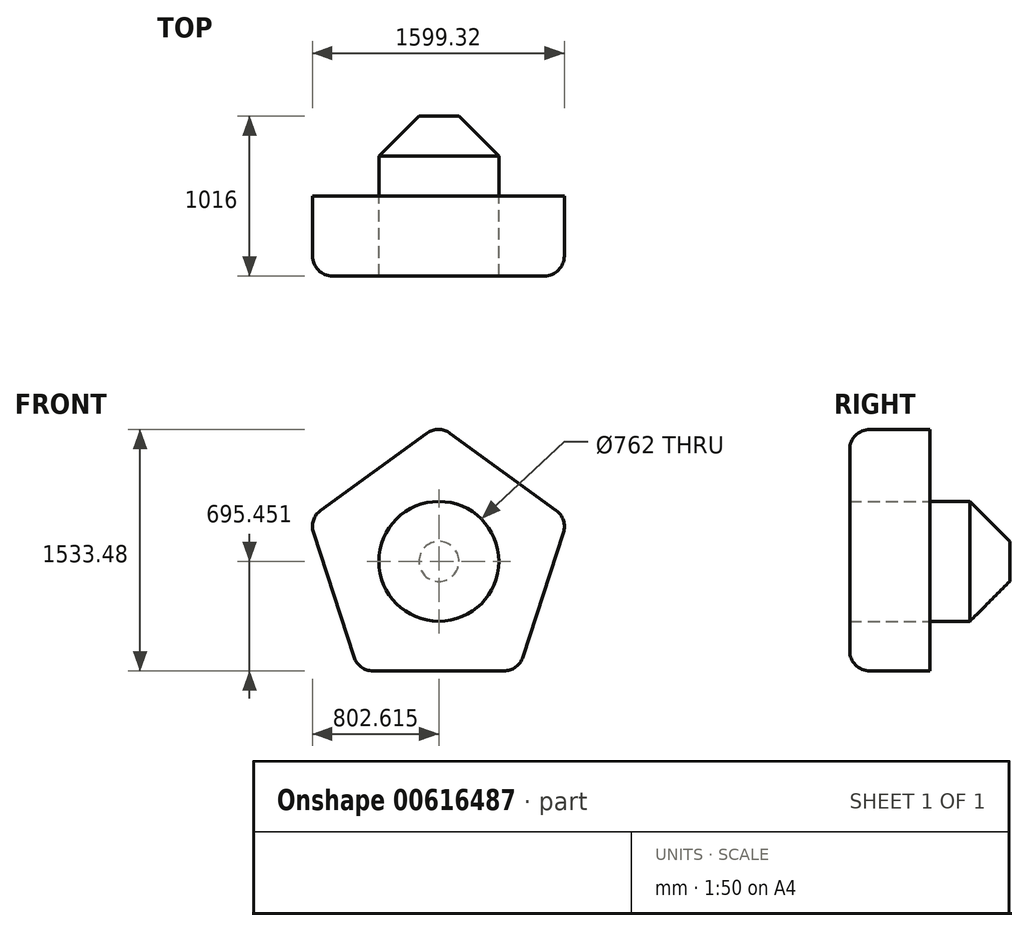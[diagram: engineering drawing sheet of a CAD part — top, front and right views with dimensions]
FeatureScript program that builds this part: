
annotation { "Feature Type Name" : "Feature", "Feature Type Description" : "" }
export const myFeature = defineFeature(function(context is Context, id is Id, definition is map)
    precondition{}
    {
        {
            var Q0;
            Q0=qCreatedBy(makeId("Front.planeOp"),FACE);
            var sketch = newSketch(context, id + "F0", { "sketchPlane" : qUnion([Q0])});
            skCircle(sketch, "E0.cCircle", {"center": v(0, 0) * mm, "radius": 699.2 * mm, "construction": true});
            skLineSegment(sketch, "E0.0", {"start": v(508, -699.2) * mm, "end": v(-508, -699.2) * mm});
            skLineSegment(sketch, "E0.1", {"start": v(-508, -699.2) * mm, "end": v(-821.96, 267.07) * mm});
            skLineSegment(sketch, "E0.2", {"start": v(-821.96, 267.07) * mm, "end": v(0, 864.26) * mm});
            skLineSegment(sketch, "E0.3", {"start": v(0, 864.26) * mm, "end": v(821.96, 267.07) * mm});
            skLineSegment(sketch, "E0.4", {"start": v(821.96, 267.07) * mm, "end": v(508, -699.2) * mm});
            skPoint(sketch, "E0.0.midPoint", {"position": v(0, -699.2) * mm});
            skCircle(sketch, "E1", {"center": v(2.96, -3.75) * mm, "radius": 381 * mm});
            skSolve(sketch);
        }
        {
            var Q0;
            Q0=makeQuery(id+"F0.imprint","IMPRINT",FACE,{"disambiguationData":[TD([[makeQuery(id+"F0.imprint","IMPRINT",EDGE,{"derivedFrom":sQuery(id+"F0.wireOp",EDGE,"E0.0")}),-1.0]])]});
            extrude(context, id + "F1", {"entities" : qUnion([Q0]), "depth" : 508 * mm, "offsetDistance" : 25.4 * mm});
        }
        {
            var Q0;
            Q0=makeQuery(id+"F1.opExtrude","SWEPT_EDGE",EDGE,{"disambiguationData":[OSD([sQuery(id+"F0.wireOp",EDGE,"E0.0"),sQuery(id+"F0.wireOp",EDGE,"E0.4")])]});
            var Q1;
            Q1=makeQuery(id+"F1.opExtrude","SWEPT_EDGE",EDGE,{"disambiguationData":[OSD([sQuery(id+"F0.wireOp",EDGE,"E0.3"),sQuery(id+"F0.wireOp",EDGE,"E0.4")])]});
            var Q2;
            Q2=makeQuery(id+"F1.opExtrude","SWEPT_EDGE",EDGE,{"disambiguationData":[OSD([sQuery(id+"F0.wireOp",EDGE,"E0.2"),sQuery(id+"F0.wireOp",EDGE,"E0.3")])]});
            var Q3;
            Q3=makeQuery(id+"F1.opExtrude","SWEPT_EDGE",EDGE,{"disambiguationData":[OSD([sQuery(id+"F0.wireOp",EDGE,"E0.1"),sQuery(id+"F0.wireOp",EDGE,"E0.2")])]});
            var Q4;
            Q4=makeQuery(id+"F1.opExtrude","SWEPT_EDGE",EDGE,{"disambiguationData":[OSD([sQuery(id+"F0.wireOp",EDGE,"E0.0"),sQuery(id+"F0.wireOp",EDGE,"E0.1")])]});
            var Q5;
            Q5=makeQuery(id+"F1.opExtrude","CAP_EDGE",EDGE,{"disambiguationData":[OSD([sQuery(id+"F0.wireOp",EDGE,"E0.0")])],"isStart":false});
            var Q6;
            Q6=makeQuery(id+"F1.opExtrude","CAP_EDGE",EDGE,{"disambiguationData":[OSD([sQuery(id+"F0.wireOp",EDGE,"E0.4")])],"isStart":false});
            var Q7;
            Q7=makeQuery(id+"F1.opExtrude","CAP_EDGE",EDGE,{"disambiguationData":[OSD([sQuery(id+"F0.wireOp",EDGE,"E0.3")])],"isStart":false});
            var Q8;
            Q8=makeQuery(id+"F1.opExtrude","CAP_EDGE",EDGE,{"disambiguationData":[OSD([sQuery(id+"F0.wireOp",EDGE,"E0.2")])],"isStart":false});
            var Q9;
            Q9=makeQuery(id+"F1.opExtrude","CAP_EDGE",EDGE,{"disambiguationData":[OSD([sQuery(id+"F0.wireOp",EDGE,"E0.1")])],"isStart":false});
            fillet(context, id + "F2", {"entities" : qUnion([Q0, Q1, Q2, Q3, Q4, Q5, Q6, Q7, Q8, Q9]), "radius" : 127 * mm, "tangentPropagation" : true, "allowEdgeOverflow" : false});
        }
        {
            var Q0;
            Q0=makeQuery(id+"F0.imprint","IMPRINT",FACE,{"disambiguationData":[TD([[makeQuery(id+"F0.imprint","IMPRINT",EDGE,{"derivedFrom":sQuery(id+"F0.wireOp",EDGE,"E1")}),1.0]])]});
            extrude(context, id + "F3", {"entities" : qUnion([Q0]), "operationType" : NewBodyOperationType.ADD, "oppositeDirection" : true, "depth" : 508 * mm, "offsetDistance" : 25.4 * mm});
        }
        {
            var Q0;
            Q0=makeQuery(id+"F3.opExtrude","CAP_FACE",FACE,{"disambiguationData":[OSD([sQuery(id+"F0.wireOp",EDGE,"E1")])],"isStart":false});
            chamfer(context, id + "F4", {"entities" : qUnion([Q0]), "width" : 254 * mm, "tangentPropagation" : true});
        }
    });
